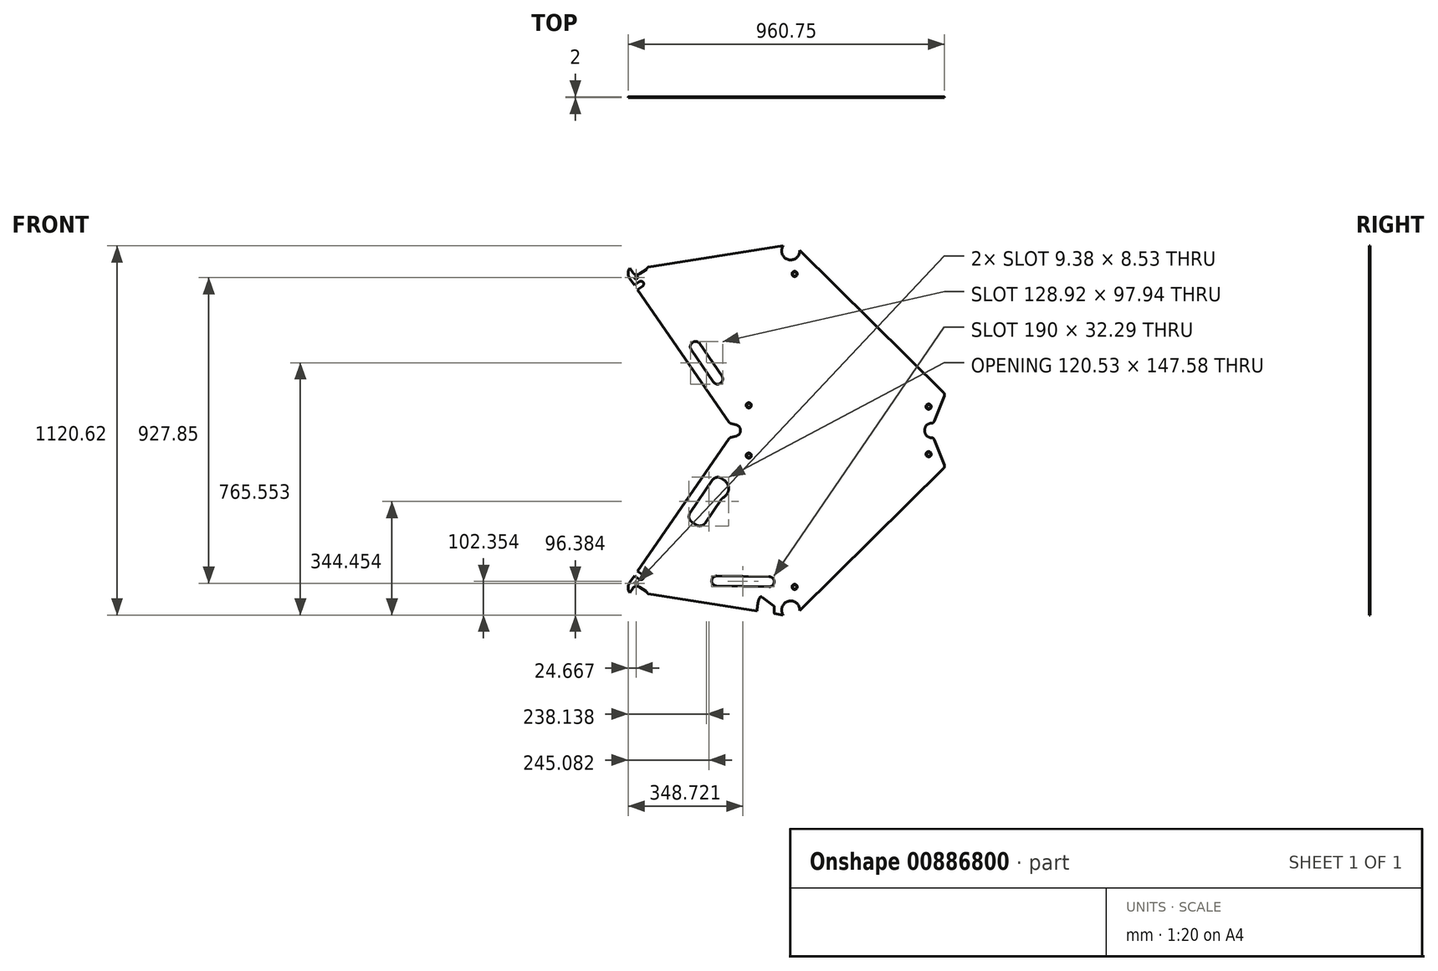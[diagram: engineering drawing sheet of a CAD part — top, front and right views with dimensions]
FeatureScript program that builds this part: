
annotation { "Feature Type Name" : "Feature", "Feature Type Description" : "" }
export const myFeature = defineFeature(function(context is Context, id is Id, definition is map)
    precondition{}
    {
        {
            var Q0;
            Q0=qCreatedBy(makeId("Front.planeOp"),FACE);
            var sketch = newSketch(context, id + "F0", { "sketchPlane" : qUnion([Q0])});
            skCircle(sketch, "E0", {"center": v(1053.9, -134.2) * mm, "radius": 17 * mm, "construction": true});
            skCircle(sketch, "E1", {"center": v(1053.9, -134.2) * mm, "radius": 21.5 * mm, "construction": true});
            skLineSegment(sketch, "E2", {"start": v(622.48, -20.32) * mm, "end": v(871.92, 345.36) * mm, "construction": true});
            skLineSegment(sketch, "E3", {"start": v(615.02, -14.4) * mm, "end": v(879.24, 372.95) * mm, "construction": true});
            skLineSegment(sketch, "E4", {"start": v(1053.9, -134.22) * mm, "end": v(865.03, 414.2) * mm, "construction": true});
            skLineSegment(sketch, "E5", {"start": v(1034.15, -125.7) * mm, "end": v(850, 409.01) * mm, "construction": true});
            skLineSegment(sketch, "E6", {"start": v(861.66, 381.3) * mm, "end": v(851.9, 409.67) * mm, "construction": true});
            skLineSegment(sketch, "E7", {"start": v(1064.21, -115.34) * mm, "end": v(880.07, 419.37) * mm, "construction": true});
            skLineSegment(sketch, "E8", {"start": v(1053.9, -134.2) * mm, "end": v(645.8, -73.78) * mm, "construction": true});
            skLineSegment(sketch, "E9", {"start": v(743.09, -99.4) * mm, "end": v(644.17, -84.76) * mm, "construction": true});
            skLineSegment(sketch, "E10", {"start": v(746.34, -77.44) * mm, "end": v(647.42, -62.8) * mm, "construction": true});
            skLineSegment(sketch, "E11", {"start": v(1035.36, -145.1) * mm, "end": v(841.66, -116.43) * mm, "construction": true});
            skLineSegment(sketch, "E12", {"start": v(1039.32, -118.4) * mm, "end": v(845.61, -89.72) * mm, "construction": true});
            skLineSegment(sketch, "E13", {"start": v(966.15, -134.86) * mm, "end": v(995.58, -139.21) * mm, "construction": true});
            skLineSegment(sketch, "E14", {"start": v(960.23, -139.03) * mm, "end": v(994.85, -144.16) * mm, "construction": true});
            skLineSegment(sketch, "E15", {"start": v(963.6, -143.58) * mm, "end": v(964.04, -140.6) * mm, "construction": true});
            skArc(sketch, "E16", {"start": v(959.64, -143) * mm, "mid": v(959.83, -143.73) * mm, "end": v(960.48, -144.13) * mm, "construction": true});
            skLineSegment(sketch, "E17", {"start": v(960.48, -144.13) * mm, "end": v(962.46, -144.42) * mm, "construction": true});
            skArc(sketch, "E18", {"start": v(962.46, -144.42) * mm, "mid": v(963.2, -144.23) * mm, "end": v(963.6, -143.58) * mm, "construction": true});
            skLineSegment(sketch, "E19", {"start": v(965.3, -133.72) * mm, "end": v(967.21, -120.86) * mm, "construction": true});
            skLineSegment(sketch, "E20", {"start": v(963, -120.24) * mm, "end": v(959.64, -143) * mm, "construction": true});
            skLineSegment(sketch, "E21", {"start": v(962.42, -124.2) * mm, "end": v(966.63, -124.82) * mm, "construction": true});
            skArc(sketch, "E22", {"start": v(965.17, -139.77) * mm, "mid": v(964.43, -139.95) * mm, "end": v(964.04, -140.6) * mm, "construction": true});
            skLineSegment(sketch, "E23", {"start": v(961.7, -129.14) * mm, "end": v(965.9, -129.76) * mm, "construction": true});
            skLineSegment(sketch, "E24", {"start": v(960.08, -126.38) * mm, "end": v(968.24, -127.58) * mm, "construction": true});
            skLineSegment(sketch, "E25", {"start": v(974.82, -141.2) * mm, "end": v(975.55, -136.25) * mm, "construction": true});
            skArc(sketch, "E26", {"start": v(965.3, -133.72) * mm, "mid": v(965.5, -134.46) * mm, "end": v(966.15, -134.86) * mm, "construction": true});
            skLineSegment(sketch, "E27", {"start": v(964.14, -119.4) * mm, "end": v(966.37, -119.73) * mm, "construction": true});
            skArc(sketch, "E28", {"start": v(964.14, -119.4) * mm, "mid": v(963.4, -119.58) * mm, "end": v(963, -120.24) * mm, "construction": true});
            skArc(sketch, "E29", {"start": v(967.21, -120.86) * mm, "mid": v(967.03, -120.12) * mm, "end": v(966.37, -119.73) * mm, "construction": true});
            skLineSegment(sketch, "E30", {"start": v(995.58, -139.21) * mm, "end": v(999.8, -144.9) * mm, "construction": true});
            skLineSegment(sketch, "E31", {"start": v(979.72, -143.94) * mm, "end": v(981.04, -135.04) * mm, "construction": true});
            skArc(sketch, "E32", {"start": v(995.7, -145.3) * mm, "mid": v(995.5, -144.55) * mm, "end": v(994.85, -144.16) * mm, "construction": true});
            skArc(sketch, "E33", {"start": v(995.25, -148.26) * mm, "mid": v(995.44, -149) * mm, "end": v(996.1, -149.4) * mm, "construction": true});
            skArc(sketch, "E34", {"start": v(998.07, -149.7) * mm, "mid": v(998.82, -149.5) * mm, "end": v(999.2, -148.85) * mm, "construction": true});
            skLineSegment(sketch, "E35", {"start": v(996.1, -149.4) * mm, "end": v(998.07, -149.7) * mm, "construction": true});
            skLineSegment(sketch, "E36", {"start": v(999.2, -148.85) * mm, "end": v(999.8, -144.9) * mm, "construction": true});
            skLineSegment(sketch, "E37", {"start": v(995.25, -148.26) * mm, "end": v(995.7, -145.3) * mm, "construction": true});
            skLineSegment(sketch, "E38", {"start": v(985.2, -142.73) * mm, "end": v(985.94, -137.79) * mm, "construction": true});
            skLineSegment(sketch, "E39", {"start": v(995.47, -146.78) * mm, "end": v(993.6, -159.38) * mm, "construction": true});
            skLineSegment(sketch, "E40", {"start": v(850, 409.01) * mm, "end": v(880.07, 419.37) * mm, "construction": true});
            skLineSegment(sketch, "E41", {"start": v(859.77, 380.65) * mm, "end": v(861.66, 381.3) * mm, "construction": true});
            skLineSegment(sketch, "E42", {"start": v(1053.9, -134.22) * mm, "end": v(1520.05, 326.73) * mm, "construction": true});
            skLineSegment(sketch, "E43", {"start": v(1081.03, -129.75) * mm, "end": v(1510.36, 294.78) * mm, "construction": true});
            skLineSegment(sketch, "E44", {"start": v(1060.7, -105.14) * mm, "end": v(1497.91, 327.2) * mm, "construction": true});
            skLineSegment(sketch, "E45", {"start": v(879.24, 372.95) * mm, "end": v(1402.67, 372.95) * mm, "construction": true});
            skLineSegment(sketch, "E46", {"start": v(901.53, 357.05) * mm, "end": v(1486.45, 357.05) * mm, "construction": true});
            skLineSegment(sketch, "E47", {"start": v(890.58, 388.85) * mm, "end": v(1474.25, 388.85) * mm, "construction": true});
            skArc(sketch, "E48", {"start": v(1486.5, 356.93) * mm, "mid": v(1487.54, 375.64) * mm, "end": v(1474.25, 388.85) * mm, "construction": true});
            skArc(sketch, "E49", {"start": v(890.58, 388.85) * mm, "mid": v(888.92, 370.5) * mm, "end": v(901.53, 357.05) * mm, "construction": true});
            skArc(sketch, "E50", {"start": v(1510.36, 294.78) * mm, "mid": v(1511.76, 313.92) * mm, "end": v(1497.91, 327.2) * mm, "construction": true});
            skArc(sketch, "E51", {"start": v(919.09, -223.5) * mm, "mid": v(918.34, -223.31) * mm, "end": v(917.6, -223.13) * mm, "construction": true});
            skFitSpline(sketch, "E52", {"points": [v(871.92, 345.36) * mm, v(875.7, 355.52) * mm, v(881.2, 370.3) * mm, v(868.26, 368.37) * mm, v(864.2, 367.77) * mm], "construction": true});
            skLineSegment(sketch, "E53", {"start": v(585.54, -70.17) * mm, "end": v(605.08, -83.05) * mm, "construction": true});
            skLineSegment(sketch, "E54", {"start": v(581.24, -61.27) * mm, "end": v(613.37, -82.46) * mm, "construction": true});
            skLineSegment(sketch, "E55", {"start": v(607.46, -8.63) * mm, "end": v(607.4, -8.7) * mm, "construction": true});
            skLineSegment(sketch, "E56", {"start": v(644.18, -84.66) * mm, "end": v(644.29, -83.94) * mm, "construction": true});
            skLineSegment(sketch, "E57", {"start": v(594.91, -64.3) * mm, "end": v(615.35, -77.77) * mm});
            skLineSegment(sketch, "E58", {"start": v(644.18, -84.66) * mm, "end": v(622.6, -81.46) * mm, "construction": true});
            skArc(sketch, "E59", {"start": v(644.63, -83.68) * mm, "mid": v(644.4, -83.74) * mm, "end": v(644.29, -83.94) * mm, "construction": true});
            skLineSegment(sketch, "E60", {"start": v(644.18, -84.66) * mm, "end": v(644.19, -84.63) * mm, "construction": true});
            skArc(sketch, "E61", {"start": v(617.78, -52.64) * mm, "mid": v(628.06, -58.54) * mm, "end": v(639.47, -61.73) * mm, "construction": true});
            skLineSegment(sketch, "E62", {"start": v(670.48, -77.43) * mm, "end": v(577.33, -63.64) * mm, "construction": true});
            skLineSegment(sketch, "E63", {"start": v(647.4, -62.9) * mm, "end": v(639.47, -61.73) * mm, "construction": true});
            skArc(sketch, "E64", {"start": v(647.3, -63.56) * mm, "mid": v(647.36, -63.78) * mm, "end": v(647.56, -63.9) * mm, "construction": true});
            skLineSegment(sketch, "E65", {"start": v(647.3, -63.56) * mm, "end": v(647.4, -62.9) * mm, "construction": true});
            skArc(sketch, "E66", {"start": v(614, -32.51) * mm, "mid": v(611.92, -43.32) * mm, "end": v(617.78, -52.64) * mm, "construction": true});
            skLineSegment(sketch, "E67", {"start": v(614, -32.51) * mm, "end": v(622.56, -20.17) * mm, "construction": true});
            skLineSegment(sketch, "E68", {"start": v(576.98, -64.11) * mm, "end": v(629.71, 4.8) * mm, "construction": true});
            skArc(sketch, "E69", {"start": v(572.75, -54.03) * mm, "mid": v(569.56, -71.65) * mm, "end": v(582.02, -84.5) * mm, "construction": true});
            skLineSegment(sketch, "E70", {"start": v(607.46, -8.63) * mm, "end": v(608.42, -9.36) * mm, "construction": true});
            skArc(sketch, "E71", {"start": v(621.55, -19.02) * mm, "mid": v(621.5, -19.24) * mm, "end": v(621.6, -19.44) * mm, "construction": true});
            skLineSegment(sketch, "E72", {"start": v(621.6, -19.44) * mm, "end": v(622.56, -20.17) * mm, "construction": true});
            skArc(sketch, "E73", {"start": v(608.42, -9.36) * mm, "mid": v(608.64, -9.42) * mm, "end": v(608.84, -9.3) * mm, "construction": true});
            skLineSegment(sketch, "E74", {"start": v(608.42, -9.36) * mm, "end": v(607.46, -8.63) * mm, "construction": true});
            skLineSegment(sketch, "E75", {"start": v(619.71, -24.29) * mm, "end": v(604.42, -12.6) * mm, "construction": true});
            skCircle(sketch, "E76", {"center": v(600.85, -74.2) * mm, "radius": 5 * mm, "construction": true});
            skLineSegment(sketch, "E77", {"start": v(621.6, -19.44) * mm, "end": v(608.42, -9.36) * mm, "construction": true});
            skLineSegment(sketch, "E78", {"start": v(841.66, -116.43) * mm, "end": v(743.09, -99.4) * mm, "construction": true});
            skLineSegment(sketch, "E79", {"start": v(746.34, -77.44) * mm, "end": v(845.61, -89.72) * mm, "construction": true});
            skEllipse(sketch, "E80", {"center": v(843.64, -103.07) * mm, "majorRadius": 13.5 * mm, "minorRadius": 8.5 * mm, "majorAxis": v(-0.15, -0.99), "construction": true});
            skCircle(sketch, "E81", {"center": v(795.03, 249.5) * mm, "radius": 9.5 * mm, "construction": true});
            skLineSegment(sketch, "E82", {"start": v(796.02, 244.3) * mm, "end": v(795.95, 244.64) * mm, "construction": true});
            skLineSegment(sketch, "E83", {"start": v(796.02, 244.3) * mm, "end": v(789.82, 248.52) * mm, "construction": true});
            skLineSegment(sketch, "E84", {"start": v(784, 242.2) * mm, "end": v(792.26, 236.56) * mm, "construction": true});
            skLineSegment(sketch, "E85", {"start": v(792.26, 236.56) * mm, "end": v(793.8, 238.84) * mm, "construction": true});
            skLineSegment(sketch, "E86", {"start": v(791.91, 236.5) * mm, "end": v(792.26, 236.56) * mm, "construction": true});
            skLineSegment(sketch, "E87", {"start": v(795.95, 244.64) * mm, "end": v(790.17, 248.58) * mm, "construction": true});
            skLineSegment(sketch, "E88", {"start": v(791.91, 236.5) * mm, "end": v(784.06, 241.85) * mm, "construction": true});
            skLineSegment(sketch, "E89", {"start": v(789.96, 238.43) * mm, "end": v(794.75, 245.46) * mm, "construction": true});
            skLineSegment(sketch, "E90", {"start": v(790.2, 238) * mm, "end": v(795.12, 245.2) * mm, "construction": true});
            skLineSegment(sketch, "E91", {"start": v(793.8, 238.84) * mm, "end": v(785.55, 244.47) * mm, "construction": true});
            skLineSegment(sketch, "E92", {"start": v(792.78, 239.54) * mm, "end": v(796.02, 244.3) * mm, "construction": true});
            skArc(sketch, "E93", {"start": v(962.06, -126.67) * mm, "mid": v(930.44, 82.62) * mm, "end": v(787.99, 239.18) * mm, "construction": true});
            skLineSegment(sketch, "E94", {"start": v(702.12, -93.34) * mm, "end": v(670.46, -88.65) * mm, "construction": true});
            skCircle(sketch, "E95", {"center": v(1053.9, -134.2) * mm, "radius": 94.9 * mm, "construction": true});
            skCircle(sketch, "E96", {"center": v(600.85, -74.2) * mm, "radius": 41.4 * mm, "construction": true});
            skLineSegment(sketch, "E97", {"start": v(1055.81, -39.3) * mm, "end": v(601.44, -32.8) * mm, "construction": true});
            skLineSegment(sketch, "E98", {"start": v(1469.36, 401.56) * mm, "end": v(1507.64, 416.26) * mm, "construction": true});
            skLineSegment(sketch, "E99", {"start": v(1507.64, 416.26) * mm, "end": v(1552.44, 299.56) * mm, "construction": true});
            skLineSegment(sketch, "E100", {"start": v(1552.44, 299.56) * mm, "end": v(1514.16, 284.87) * mm, "construction": true});
            skLineSegment(sketch, "E101", {"start": v(1514.16, 284.87) * mm, "end": v(1469.36, 401.56) * mm, "construction": true});
            skLineSegment(sketch, "E102", {"start": v(1516.78, 301.13) * mm, "end": v(1081.03, -129.75) * mm, "construction": true});
            skLineSegment(sketch, "E103", {"start": v(572.75, -54.03) * mm, "end": v(878.77, 388.85) * mm, "construction": true});
            skLineSegment(sketch, "E104.trimOffspring", {"start": v(1028.21, -144.04) * mm, "end": v(617.45, -79.16) * mm, "construction": true});
            skCircle(sketch, "E105", {"center": v(926.64, 334.5) * mm, "radius": 4 * mm, "construction": true});
            skCircle(sketch, "E106", {"center": v(1472.88, 338.55) * mm, "radius": 4 * mm, "construction": true});
            skCircle(sketch, "E107", {"center": v(1065.9, -64.22) * mm, "radius": 4 * mm, "construction": true});
            skLineSegment(sketch, "E108", {"start": v(1053.9, -134.22) * mm, "end": v(1237.28, -134.22) * mm, "construction": true});
            skLineSegment(sketch, "E109", {"start": v(1053.9, -134.22) * mm, "end": v(1053.9, 23.55) * mm, "construction": true});
            skCircle(sketch, "E110", {"center": v(866.64, 414.5) * mm, "radius": 25 * mm, "construction": true});
            skCircle(sketch, "E111", {"center": v(1489.1, 401.54) * mm, "radius": 28.6 * mm, "construction": true});
            skLineSegment(sketch, "E112", {"start": v(1518.77, 296.07) * mm, "end": v(1482.36, 388.85) * mm, "construction": true});
            skLineSegment(sketch, "E113.trimOffspring", {"start": v(869.05, 388.85) * mm, "end": v(1487.73, 388.85) * mm});
            skCircle(sketch, "E114", {"center": v(600.85, -74.2) * mm, "radius": 312.5 * mm, "construction": true});
            skLineSegment(sketch, "E115.0", {"start": v(568.9, -54.33) * mm, "end": v(583.27, -33.52) * mm, "construction": true});
            skArc(sketch, "E116", {"start": v(568.9, -54.33) * mm, "mid": v(565.18, -65.75) * mm, "end": v(568.34, -77.35) * mm, "construction": true});
            skLineSegment(sketch, "E117.trimOffspring", {"start": v(596.35, -14.6) * mm, "end": v(875.12, 388.85) * mm});
            skArc(sketch, "E118", {"start": v(594.2, -41.07) * mm, "mid": v(610.2, -38.15) * mm, "end": v(607.28, -22.15) * mm, "construction": true});
            skLineSegment(sketch, "E119", {"start": v(600.85, -74.2) * mm, "end": v(600.85, 14.84) * mm, "construction": true});
            skLineSegment(sketch, "E120", {"start": v(594.2, -41.07) * mm, "end": v(583.27, -33.52) * mm, "construction": true});
            skLineSegment(sketch, "E121", {"start": v(607.28, -22.15) * mm, "end": v(596.35, -14.6) * mm, "construction": true});
            skLineSegment(sketch, "E122", {"start": v(596.35, -14.6) * mm, "end": v(592.94, -19.53) * mm});
            skLineSegment(sketch, "E123", {"start": v(592.94, -19.53) * mm, "end": v(603.87, -27.09) * mm});
            skArc(sketch, "E124", {"start": v(594.2, -41.07) * mm, "mid": v(606.03, -38.91) * mm, "end": v(603.87, -27.09) * mm});
            skLineSegment(sketch, "E125", {"start": v(583.27, -33.52) * mm, "end": v(594.2, -41.07) * mm});
            skArc(sketch, "E126", {"start": v(587.4, -59.34) * mm, "mid": v(582.89, -58.47) * mm, "end": v(579.09, -61.05) * mm, "construction": true});
            skLineSegment(sketch, "E127", {"start": v(585.72, -29.98) * mm, "end": v(593.74, -35.53) * mm, "construction": true});
            skLineSegment(sketch, "E128", {"start": v(599.04, -34.08) * mm, "end": v(590.57, -28.23) * mm, "construction": true});
            skArc(sketch, "E129", {"start": v(585.51, -49.43) * mm, "mid": v(580.66, -50.42) * mm, "end": v(581.66, -55.27) * mm});
            skLineSegment(sketch, "E130", {"start": v(574.13, -68.56) * mm, "end": v(565.36, -81.86) * mm});
            skLineSegment(sketch, "E131", {"start": v(568.9, -54.33) * mm, "end": v(579.09, -61.05) * mm, "construction": true});
            skLineSegment(sketch, "E132.0", {"start": v(1031.07, -149.56) * mm, "end": v(621.61, -84.88) * mm});
            skLineSegment(sketch, "E133", {"start": v(617.45, -79.16) * mm, "end": v(617.45, -79.16) * mm});
            skPoint(sketch, "E134.visualSharp", {"position": v(616.67, -84.1) * mm});
            skArc(sketch, "E134.filletArc", {"start": v(617.5, -80.94) * mm, "mid": v(618.94, -83.55) * mm, "end": v(621.61, -84.88) * mm});
            skPoint(sketch, "E135.visualSharp", {"position": v(617.45, -79.16) * mm});
            skArc(sketch, "E135.filletArc", {"start": v(617.5, -80.94) * mm, "mid": v(616.74, -79.14) * mm, "end": v(615.35, -77.77) * mm});
            skLineSegment(sketch, "E136.0", {"start": v(592.24, -11.75) * mm, "end": v(869.05, 388.85) * mm});
            skLineSegment(sketch, "E137.0", {"start": v(592.24, -11.75) * mm, "end": v(588.82, -16.69) * mm});
            skLineSegment(sketch, "E138", {"start": v(588.82, -16.69) * mm, "end": v(592.94, -19.53) * mm});
            skLineSegment(sketch, "E139.0", {"start": v(564.78, -51.48) * mm, "end": v(579.16, -30.67) * mm});
            skArc(sketch, "E140.0", {"start": v(564.78, -51.48) * mm, "mid": v(560.18, -66.76) * mm, "end": v(565.36, -81.86) * mm});
            skLineSegment(sketch, "E141.0", {"start": v(568.8, -54.26) * mm, "end": v(583.18, -33.46) * mm, "construction": true});
            skArc(sketch, "E141.1", {"start": v(568.8, -54.26) * mm, "mid": v(565.07, -65.75) * mm, "end": v(568.24, -77.4) * mm, "construction": true});
            skLineSegment(sketch, "E142", {"start": v(579.16, -30.67) * mm, "end": v(583.27, -33.52) * mm});
            skLineSegment(sketch, "E143.0", {"start": v(1081.3, -136.52) * mm, "end": v(1522.64, 299.9) * mm});
            skLineSegment(sketch, "E144.0", {"start": v(1522.64, 299.9) * mm, "end": v(1487.73, 388.85) * mm});
            skArc(sketch, "E145", {"start": v(1081.3, -136.52) * mm, "mid": v(1046.98, -107.57) * mm, "end": v(1031.07, -149.56) * mm});
            skPoint(sketch, "E146.newPointB", {"position": v(587.4, -59.34) * mm});
            skArc(sketch, "E146.filletArc", {"start": v(594.91, -64.3) * mm, "mid": v(583.64, -62.12) * mm, "end": v(574.13, -68.56) * mm});
            skLineSegment(sketch, "E147", {"start": v(583.58, -52.35) * mm, "end": v(581.66, -55.27) * mm, "construction": true});
            skLineSegment(sketch, "E148", {"start": v(583.58, -52.35) * mm, "end": v(585.51, -49.43) * mm, "construction": true});
            skLineSegment(sketch, "E149", {"start": v(581.66, -55.27) * mm, "end": v(584.16, -56.92) * mm});
            skLineSegment(sketch, "E150", {"start": v(585.51, -49.43) * mm, "end": v(588.02, -51.08) * mm});
            skArc(sketch, "E151", {"start": v(584.16, -56.92) * mm, "mid": v(589.01, -55.93) * mm, "end": v(588.02, -51.08) * mm});
            skPoint(sketch, "E152", {"position": v(553.54, -71.95) * mm});
            skSolve(sketch);
        }
        {
            var Q0;
            Q0=qSketchRegion(id+"F0",true);
            extrude(context, id + "F1", {"entities" : qUnion([Q0]), "depth" : 2 * mm, "offsetDistance" : 25 * mm});
        }
        {
            var Q0;
            Q0=makeQuery(id+"F1.opExtrude","SWEPT_FACE",FACE,{"disambiguationData":[OSD([sQuery(id+"F0.wireOp",EDGE,"E113.trimOffspring")])]});
            cPlane(context, id + "F2", {"entities" : qUnion([Q0]), "cplaneType" : CPlaneType.OFFSET, "offset" : 21.9 * mm, "width" : 150 * mm, "height" : 150 * mm});
        }
        {
            var Q0;
            Q0=makeQuery(id+"F1.opExtrude","SWEPT_BODY",BODY,{"disambiguationData":[OSD([sQuery(id+"F0.wireOp",EDGE,"a49be1ca-efc1-4c5e-93b1-82285a78bd7e"),sQuery(id+"F0.wireOp",EDGE,"E53"),sQuery(id+"F0.wireOp",EDGE,"00abc04f-36b8-44c4-b012-511981e3aebb"),sQuery(id+"F0.wireOp",EDGE,"E57"),sQuery(id+"F0.wireOp",EDGE,"c0fece56-cd10-4327-9040-2cab23e675d4"),sQuery(id+"F0.wireOp",EDGE,"81bee024-3d0e-4fca-8609-8fb9e83f8aac"),sQuery(id+"F0.wireOp",EDGE,"E69"),sQuery(id+"F0.wireOp",EDGE,"PVY0APLz-6rdr-JrDk-CvCb-vWmYWycaJObT"),sQuery(id+"F0.wireOp",EDGE,"rSiPkJzu-22ck-wLmw-T34Z-YrS7vC3DeLN9"),sQuery(id+"F0.wireOp",EDGE,"E102"),sQuery(id+"F0.wireOp",EDGE,"E103"),sQuery(id+"F0.wireOp",EDGE,"YospaPRb-7m9c-EU3X-92Vu-9KYmre8nDPZu"),sQuery(id+"F0.wireOp",EDGE,"E104.trimOffspring")])]});
            var Q1;
            Q1=qCreatedBy(id+"F2.planeOp",FACE);
            mirror(context, id + "F3", {"entities" : qUnion([Q0]), "mirrorPlane" : qUnion([Q1])});
        }
        {
            var Q0;
            Q0=makeQuery(id+"F1.opExtrude","CAP_FACE",FACE,{"disambiguationData":[OSD([sQuery(id+"F0.wireOp",EDGE,"a49be1ca-efc1-4c5e-93b1-82285a78bd7e"),sQuery(id+"F0.wireOp",EDGE,"E53"),sQuery(id+"F0.wireOp",EDGE,"00abc04f-36b8-44c4-b012-511981e3aebb"),sQuery(id+"F0.wireOp",EDGE,"E57"),sQuery(id+"F0.wireOp",EDGE,"c0fece56-cd10-4327-9040-2cab23e675d4"),sQuery(id+"F0.wireOp",EDGE,"81bee024-3d0e-4fca-8609-8fb9e83f8aac"),sQuery(id+"F0.wireOp",EDGE,"E69"),sQuery(id+"F0.wireOp",EDGE,"PVY0APLz-6rdr-JrDk-CvCb-vWmYWycaJObT"),sQuery(id+"F0.wireOp",EDGE,"rSiPkJzu-22ck-wLmw-T34Z-YrS7vC3DeLN9"),sQuery(id+"F0.wireOp",EDGE,"E102"),sQuery(id+"F0.wireOp",EDGE,"E103"),sQuery(id+"F0.wireOp",EDGE,"YospaPRb-7m9c-EU3X-92Vu-9KYmre8nDPZu"),sQuery(id+"F0.wireOp",EDGE,"E104.trimOffspring")])],"isStart":false});
            var sketch = newSketch(context, id + "F4", { "sketchPlane" : qUnion([Q0])});
            skLineSegment(sketch, "E153", {"start": v(884.05, 410.75) * mm, "end": v(1482.9, 410.75) * mm, "construction": true});
            skLineSegment(sketch, "E154", {"start": v(869.05, 388.85) * mm, "end": v(903.47, 301.13) * mm, "construction": true});
            skArc(sketch, "E155", {"start": v(888.38, 393.8) * mm, "mid": v(901.55, 410.75) * mm, "end": v(888.38, 427.7) * mm});
            skLineSegment(sketch, "E156", {"start": v(869.05, 388.85) * mm, "end": v(869.05, 388.85) * mm});
            skLineSegment(sketch, "E157", {"start": v(1477.73, 432.65) * mm, "end": v(869.05, 432.65) * mm});
            skLineSegment(sketch, "E158", {"start": v(869.05, 432.65) * mm, "end": v(888.38, 427.7) * mm});
            skLineSegment(sketch, "E159", {"start": v(869.05, 388.85) * mm, "end": v(888.38, 393.8) * mm});
            skLineSegment(sketch, "E160", {"start": v(1477.73, 388.85) * mm, "end": v(869.05, 388.85) * mm});
            skArc(sketch, "E161", {"start": v(1477.73, 432.65) * mm, "mid": v(1460.4, 410.75) * mm, "end": v(1477.73, 388.85) * mm});
            skSolve(sketch);
        }
        {
            var Q0;
            Q0=qSketchRegion(id+"F4",true);
            var Q1;
            Q1=makeQuery(id+"F3.opPattern","COPY",FACE,{"derivedFrom":makeQuery(id+"F1.opExtrude","CAP_FACE",FACE,{"disambiguationData":[OSD([sQuery(id+"F0.wireOp",EDGE,"a49be1ca-efc1-4c5e-93b1-82285a78bd7e"),sQuery(id+"F0.wireOp",EDGE,"E53"),sQuery(id+"F0.wireOp",EDGE,"00abc04f-36b8-44c4-b012-511981e3aebb"),sQuery(id+"F0.wireOp",EDGE,"E57"),sQuery(id+"F0.wireOp",EDGE,"c0fece56-cd10-4327-9040-2cab23e675d4"),sQuery(id+"F0.wireOp",EDGE,"81bee024-3d0e-4fca-8609-8fb9e83f8aac"),sQuery(id+"F0.wireOp",EDGE,"E69"),sQuery(id+"F0.wireOp",EDGE,"PVY0APLz-6rdr-JrDk-CvCb-vWmYWycaJObT"),sQuery(id+"F0.wireOp",EDGE,"rSiPkJzu-22ck-wLmw-T34Z-YrS7vC3DeLN9"),sQuery(id+"F0.wireOp",EDGE,"E102"),sQuery(id+"F0.wireOp",EDGE,"E103"),sQuery(id+"F0.wireOp",EDGE,"YospaPRb-7m9c-EU3X-92Vu-9KYmre8nDPZu"),sQuery(id+"F0.wireOp",EDGE,"E104.trimOffspring")])],"isStart":true}),"instanceName":"1"});
            extrude(context, id + "F5", {"entities" : qUnion([Q0]), "operationType" : NewBodyOperationType.ADD, "endBound" : BoundingType.UP_TO_SURFACE, "oppositeDirection" : true, "depth" : 65 * mm, "endBoundEntityFace" : qUnion([Q1]), "offsetDistance" : 25 * mm});
        }
        {
            var Q0;
            {var subQ0=sQuery(id+"F4.wireOp",EDGE,"E160");Q0=makeQuery(id+"F4.imprint","IMPRINT",FACE,{"disambiguationData":[TD([[makeQuery(id+"F4.imprint","IMPRINT",EDGE,{"derivedFrom":subQ0}),-1.0]])]});}
            var sketch = newSketch(context, id + "F6", { "sketchPlane" : qUnion([Q0])});
            skLineSegment(sketch, "E162.bottom", {"start": v(829.1, -31.06) * mm, "end": v(989.1, -33.35) * mm});
            skLineSegment(sketch, "E162.top", {"start": v(828.68, -61.06) * mm, "end": v(988.68, -63.35) * mm});
            skArc(sketch, "E163", {"start": v(829.1, -31.06) * mm, "mid": v(813.9, -45.85) * mm, "end": v(828.68, -61.06) * mm});
            skArc(sketch, "E164", {"start": v(988.68, -63.35) * mm, "mid": v(1003.89, -48.57) * mm, "end": v(989.1, -33.35) * mm});
            skCircle(sketch, "E165", {"center": v(1053.9, -134.22) * mm, "radius": 101.64 * mm, "construction": true});
            skPoint(sketch, "E166.0", {"position": v(1035.36, -145.1) * mm});
            skLineSegment(sketch, "E167.0", {"start": v(1035.36, -145.1) * mm, "end": v(841.66, -116.43) * mm, "construction": true});
            skPoint(sketch, "E168", {"position": v(952.27, -132.8) * mm});
            skCircle(sketch, "E169", {"center": v(1053.9, -134.22) * mm, "radius": 79.64 * mm, "construction": true});
            skPoint(sketch, "E170", {"position": v(1003.7, -140.42) * mm});
            skCircle(sketch, "E171", {"center": v(1053.9, -134.22) * mm, "radius": 50.57 * mm, "construction": true});
            skCircle(sketch, "E172", {"center": v(1053.9, -134.22) * mm, "radius": 60.57 * mm, "construction": true});
            skArc(sketch, "E173", {"start": v(959.05, -97.69) * mm, "mid": v(953.72, -117.06) * mm, "end": v(952.3, -137.11) * mm});
            skArc(sketch, "E174", {"start": v(966.67, -95.45) * mm, "mid": v(962.31, -94.68) * mm, "end": v(959.05, -97.69) * mm});
            skArc(sketch, "E175", {"start": v(1004.16, -125.06) * mm, "mid": v(1003.34, -135.24) * mm, "end": v(1004.57, -145.37) * mm});
            skPoint(sketch, "E176.visualSharp", {"position": v(995.37, -118.6) * mm});
            skPoint(sketch, "E177.visualSharp", {"position": v(1004.16, -125.06) * mm});
            skArc(sketch, "E177.filletArc", {"start": v(1004.16, -125.06) * mm, "mid": v(1004, -123.4) * mm, "end": v(1002.99, -122.1) * mm});
            skPoint(sketch, "E178", {"position": v(952.3, -137.11) * mm});
            skPoint(sketch, "E179", {"position": v(974.51, -140.62) * mm});
            skPoint(sketch, "E180", {"position": v(994.07, -143.71) * mm});
            skPoint(sketch, "E181", {"position": v(1004.57, -145.37) * mm});
            skLineSegment(sketch, "E182", {"start": v(966.67, -95.45) * mm, "end": v(1002.99, -122.1) * mm});
            skLineSegment(sketch, "E183", {"start": v(952.3, -137.11) * mm, "end": v(1004.57, -145.37) * mm});
            skSolve(sketch);
        }
        {
            var Q0;
            Q0=qSketchRegion(id+"F6",true);
            extrude(context, id + "F7", {"entities" : qUnion([Q0]), "operationType" : NewBodyOperationType.REMOVE, "oppositeDirection" : true, "depth" : 25 * mm, "offsetDistance" : 25 * mm});
        }
        {
            var Q0;
            {var subQ0=sQuery(id+"F4.wireOp",EDGE,"E160");Q0=makeQuery(id+"F4.imprint","IMPRINT",FACE,{"disambiguationData":[TD([[makeQuery(id+"F4.imprint","IMPRINT",EDGE,{"derivedFrom":subQ0}),-1.0]])]});}
            var sketch = newSketch(context, id + "F8", { "sketchPlane" : qUnion([Q0])});
            skLineSegment(sketch, "E184", {"start": v(748.46, 160.82) * mm, "end": v(816.08, 259.96) * mm});
            skLineSegment(sketch, "E185", {"start": v(843.88, 265.2) * mm, "end": v(852.14, 259.57) * mm});
            skLineSegment(sketch, "E186", {"start": v(766.1, 124.58) * mm, "end": v(753.71, 133.03) * mm});
            skCircle(sketch, "E187.0", {"center": v(600.85, -74.2) * mm, "radius": 312.5 * mm, "construction": true});
            skLineSegment(sketch, "E187.1", {"start": v(622.48, -20.32) * mm, "end": v(871.92, 345.36) * mm, "construction": true});
            skLineSegment(sketch, "E188.0", {"start": v(884.05, 410.75) * mm, "end": v(1482.9, 410.75) * mm, "construction": true});
            skCircle(sketch, "E189.MirrorC", {"center": v(600.85, 895.7) * mm, "radius": 312.5 * mm, "construction": true});
            skLineSegment(sketch, "E190.MirrorCS", {"start": v(622.48, 841.82) * mm, "end": v(871.92, 476.13) * mm, "construction": true});
            skLineSegment(sketch, "E191", {"start": v(818.34, 558.24) * mm, "end": v(751.84, 655.72) * mm});
            skLineSegment(sketch, "E192", {"start": v(756.04, 677.95) * mm, "end": v(756.04, 677.95) * mm});
            skLineSegment(sketch, "E193", {"start": v(778.28, 673.75) * mm, "end": v(844.77, 576.27) * mm});
            skLineSegment(sketch, "E194", {"start": v(840.57, 554.04) * mm, "end": v(840.57, 554.04) * mm});
            skLineSegment(sketch, "E195.0", {"start": v(797.53, 236.3) * mm, "end": v(785.55, 244.47) * mm, "construction": true});
            skLineSegment(sketch, "E196.MirrorCS", {"start": v(797.53, 585.2) * mm, "end": v(785.55, 577.03) * mm, "construction": true});
            skLineSegment(sketch, "E197", {"start": v(797.53, 585.2) * mm, "end": v(768.19, 565.19) * mm, "construction": true});
            skPoint(sketch, "E198.orphan", {"position": v(793.8, 582.66) * mm});
            skPoint(sketch, "E199.orphan", {"position": v(793.8, 238.84) * mm});
            skLineSegment(sketch, "E200", {"start": v(797.53, 236.3) * mm, "end": v(778.55, 249.24) * mm, "construction": true});
            skPoint(sketch, "E201.visualSharp", {"position": v(827.35, 276.48) * mm});
            skArc(sketch, "E201.filletArc", {"start": v(843.88, 265.2) * mm, "mid": v(828.9, 268.34) * mm, "end": v(816.08, 259.96) * mm});
            skPoint(sketch, "E202.visualSharp", {"position": v(872.79, 245.49) * mm});
            skArc(sketch, "E202.filletArc", {"start": v(849.3, 207.03) * mm, "mid": v(865.52, 232.5) * mm, "end": v(852.14, 259.57) * mm});
            skPoint(sketch, "E203.visualSharp", {"position": v(737.2, 144.3) * mm});
            skArc(sketch, "E203.filletArc", {"start": v(748.46, 160.82) * mm, "mid": v(745.33, 145.84) * mm, "end": v(753.71, 133.03) * mm});
            skPoint(sketch, "E204.visualSharp", {"position": v(782.63, 113.3) * mm});
            skArc(sketch, "E204.filletArc", {"start": v(766.1, 124.58) * mm, "mid": v(781.09, 121.45) * mm, "end": v(793.9, 129.83) * mm});
            skPoint(sketch, "E205.visualSharp", {"position": v(742.83, 668.94) * mm});
            skArc(sketch, "E205.filletArc", {"start": v(756.04, 677.95) * mm, "mid": v(749.34, 667.7) * mm, "end": v(751.84, 655.72) * mm});
            skPoint(sketch, "E206.visualSharp", {"position": v(769.26, 686.97) * mm});
            skArc(sketch, "E206.filletArc", {"start": v(778.28, 673.75) * mm, "mid": v(768.03, 680.46) * mm, "end": v(756.04, 677.95) * mm});
            skPoint(sketch, "E207.visualSharp", {"position": v(853.79, 563.05) * mm});
            skArc(sketch, "E207.filletArc", {"start": v(840.57, 554.04) * mm, "mid": v(847.28, 564.28) * mm, "end": v(844.77, 576.27) * mm});
            skPoint(sketch, "E208.visualSharp", {"position": v(827.35, 545.02) * mm});
            skArc(sketch, "E208.filletArc", {"start": v(818.34, 558.24) * mm, "mid": v(828.58, 551.53) * mm, "end": v(840.57, 554.04) * mm});
            skLineSegment(sketch, "E209", {"start": v(793.9, 129.83) * mm, "end": v(842.22, 200.66) * mm});
            skArc(sketch, "E210", {"start": v(849.3, 207.03) * mm, "mid": v(845.38, 204.28) * mm, "end": v(842.22, 200.66) * mm});
            skSolve(sketch);
        }
        {
            var Q0;
            Q0=qSketchRegion(id+"F8",true);
            extrude(context, id + "F9", {"entities" : qUnion([Q0]), "operationType" : NewBodyOperationType.REMOVE, "endBound" : BoundingType.THROUGH_ALL, "oppositeDirection" : true, "depth" : 25 * mm, "offsetDistance" : 25 * mm});
        }
        {
            var Q0;
            {var subQ0=sQuery(id+"F4.wireOp",EDGE,"E160");Q0=makeQuery(id+"F4.imprint","IMPRINT",FACE,{"disambiguationData":[TD([[makeQuery(id+"F4.imprint","IMPRINT",EDGE,{"derivedFrom":subQ0}),-1.0]])]});}
            var sketch = newSketch(context, id + "F10", { "sketchPlane" : qUnion([Q0])});
            skPoint(sketch, "E211.0", {"position": v(926.64, 334.5) * mm});
            skPoint(sketch, "E211.1", {"position": v(1472.88, 338.55) * mm});
            skPoint(sketch, "E211.2", {"position": v(1065.9, -64.22) * mm});
            skPoint(sketch, "E212.MirrorP", {"position": v(926.64, 487) * mm});
            skPoint(sketch, "E213.MirrorP", {"position": v(1472.88, 482.95) * mm});
            skPoint(sketch, "E214.MirrorP", {"position": v(1065.9, 885.72) * mm});
            skSolve(sketch);
        }
        {
            var Q0;
            Q0=sQuery(id+"F10.wireOp",VERTEX,"E214.MirrorP");
            var Q1;
            Q1=sQuery(id+"F10.wireOp",VERTEX,"E212.MirrorP");
            var Q2;
            Q2=sQuery(id+"F10.wireOp",VERTEX,"E213.MirrorP");
            var Q3;
            Q3=sQuery(id+"F0.wireOp",VERTEX,"E105.center");
            var Q4;
            Q4=sQuery(id+"F0.wireOp",VERTEX,"E106.center");
            var Q5;
            Q5=sQuery(id+"F0.wireOp",VERTEX,"E107.center");
            var Q6;
            Q6=sQuery(id+"F10.wireOp",VERTEX,"E211.2");
            var Q7;
            Q7=sQuery(id+"F10.wireOp",VERTEX,"E211.0");
            var Q8;
            Q8=sQuery(id+"F10.wireOp",VERTEX,"E211.1");
            var Q9;
            Q9=makeQuery(id+"F1.opExtrude","SWEPT_BODY",BODY,{"disambiguationData":[OSD([sQuery(id+"F0.wireOp",EDGE,"a49be1ca-efc1-4c5e-93b1-82285a78bd7e"),sQuery(id+"F0.wireOp",EDGE,"E53"),sQuery(id+"F0.wireOp",EDGE,"00abc04f-36b8-44c4-b012-511981e3aebb"),sQuery(id+"F0.wireOp",EDGE,"E57"),sQuery(id+"F0.wireOp",EDGE,"81bee024-3d0e-4fca-8609-8fb9e83f8aac"),sQuery(id+"F0.wireOp",EDGE,"E102"),sQuery(id+"F0.wireOp",EDGE,"YospaPRb-7m9c-EU3X-92Vu-9KYmre8nDPZu"),sQuery(id+"F0.wireOp",EDGE,"E104.trimOffspring"),sQuery(id+"F0.wireOp",EDGE,"E112"),sQuery(id+"F0.wireOp",EDGE,"E113.trimOffspring"),sQuery(id+"F0.wireOp",EDGE,"E115.0"),sQuery(id+"F0.wireOp",EDGE,"E116"),sQuery(id+"F0.wireOp",EDGE,"E117.trimOffspring"),sQuery(id+"F0.wireOp",EDGE,"E118"),sQuery(id+"F0.wireOp",EDGE,"E120"),sQuery(id+"F0.wireOp",EDGE,"E121")])]});
            hole(context, id + "F11", {"style" : HoleStyle.C_SINK, "endStyle" : HoleEndStyle.THROUGH, "holeDiameter" : 8 * mm, "cSinkDiameter" : 16 * mm, "cSinkAngle" : 90 * degree, "majorDiameter" : 5 * mm, "isTappedThrough" : true, "tappedDepth" : 12 * mm, "tapClearance" : 3, "locations" : qUnion([Q0, Q1, Q2, Q3, Q4, Q5, Q6, Q7, Q8]), "scope" : qUnion([Q9])});
        }
        {
            var Q0;
            Q0=makeQuery(id+"F3.opPattern","COPY",EDGE,{"derivedFrom":makeQuery(id+"F1.opExtrude","SWEPT_EDGE",EDGE,{"disambiguationData":[OSD([sQuery(id+"F0.wireOp",EDGE,"E113.trimOffspring"),sQuery(id+"F0.wireOp",EDGE,"E144.0")])]}),"instanceName":"1"});
            var Q1;
            Q1=makeQuery(id+"F1.opExtrude","SWEPT_EDGE",EDGE,{"disambiguationData":[OSD([sQuery(id+"F0.wireOp",EDGE,"E113.trimOffspring"),sQuery(id+"F0.wireOp",EDGE,"E144.0")])]});
            var Q2;
            Q2=makeQuery(id+"F3.opPattern","COPY",EDGE,{"derivedFrom":makeQuery(id+"F1.opExtrude","SWEPT_EDGE",EDGE,{"disambiguationData":[OSD([sQuery(id+"F0.wireOp",EDGE,"E143.0"),sQuery(id+"F0.wireOp",EDGE,"E144.0")])]}),"instanceName":"1"});
            var Q3;
            Q3=makeQuery(id+"F1.opExtrude","SWEPT_EDGE",EDGE,{"disambiguationData":[OSD([sQuery(id+"F0.wireOp",EDGE,"E143.0"),sQuery(id+"F0.wireOp",EDGE,"E144.0")])]});
            var Q4;
            {var subQ0=sQuery(id+"F0.wireOp",EDGE,"E136.0");Q4=makeQuery(id+"F5.boolean.opBoolean","MERGE",EDGE,{"derivedFrom":[makeQuery(id+"F1.opExtrude","SWEPT_EDGE",EDGE,{"disambiguationData":[OSD([sQuery(id+"F0.wireOp",EDGE,"E113.trimOffspring"),subQ0])]}),makeQuery(id+"F5.opExtrude","SWEPT_EDGE",EDGE,{"disambiguationData":[OSD([subQ0,sQuery(id+"F0.wireOp",EDGE,"E137.0"),sQuery(id+"F4.wireOp",EDGE,"E159"),sQuery(id+"F4.wireOp",EDGE,"E160")])]})]});}
            var Q5;
            Q5=makeQuery(id+"F5.boolean.opBoolean","MERGE",EDGE,{"derivedFrom":[makeQuery(id+"F3.opPattern","COPY",EDGE,{"derivedFrom":makeQuery(id+"F1.opExtrude","SWEPT_EDGE",EDGE,{"disambiguationData":[OSD([sQuery(id+"F0.wireOp",EDGE,"E113.trimOffspring"),sQuery(id+"F0.wireOp",EDGE,"E136.0")])]}),"instanceName":"1"}),makeQuery(id+"F5.opExtrude","SWEPT_EDGE",EDGE,{"disambiguationData":[OSD([sQuery(id+"F4.wireOp",EDGE,"E157"),sQuery(id+"F4.wireOp",EDGE,"E158")])]})]});
            fillet(context, id + "F12", {"entities" : qUnion([Q0, Q1, Q2, Q3, Q4, Q5]), "tangentPropagation" : true, "radius" : 10 * mm, "defaultsChanged" : false, "vertexSettings" : [], "allowEdgeOverflow" : false});
        }
    });
